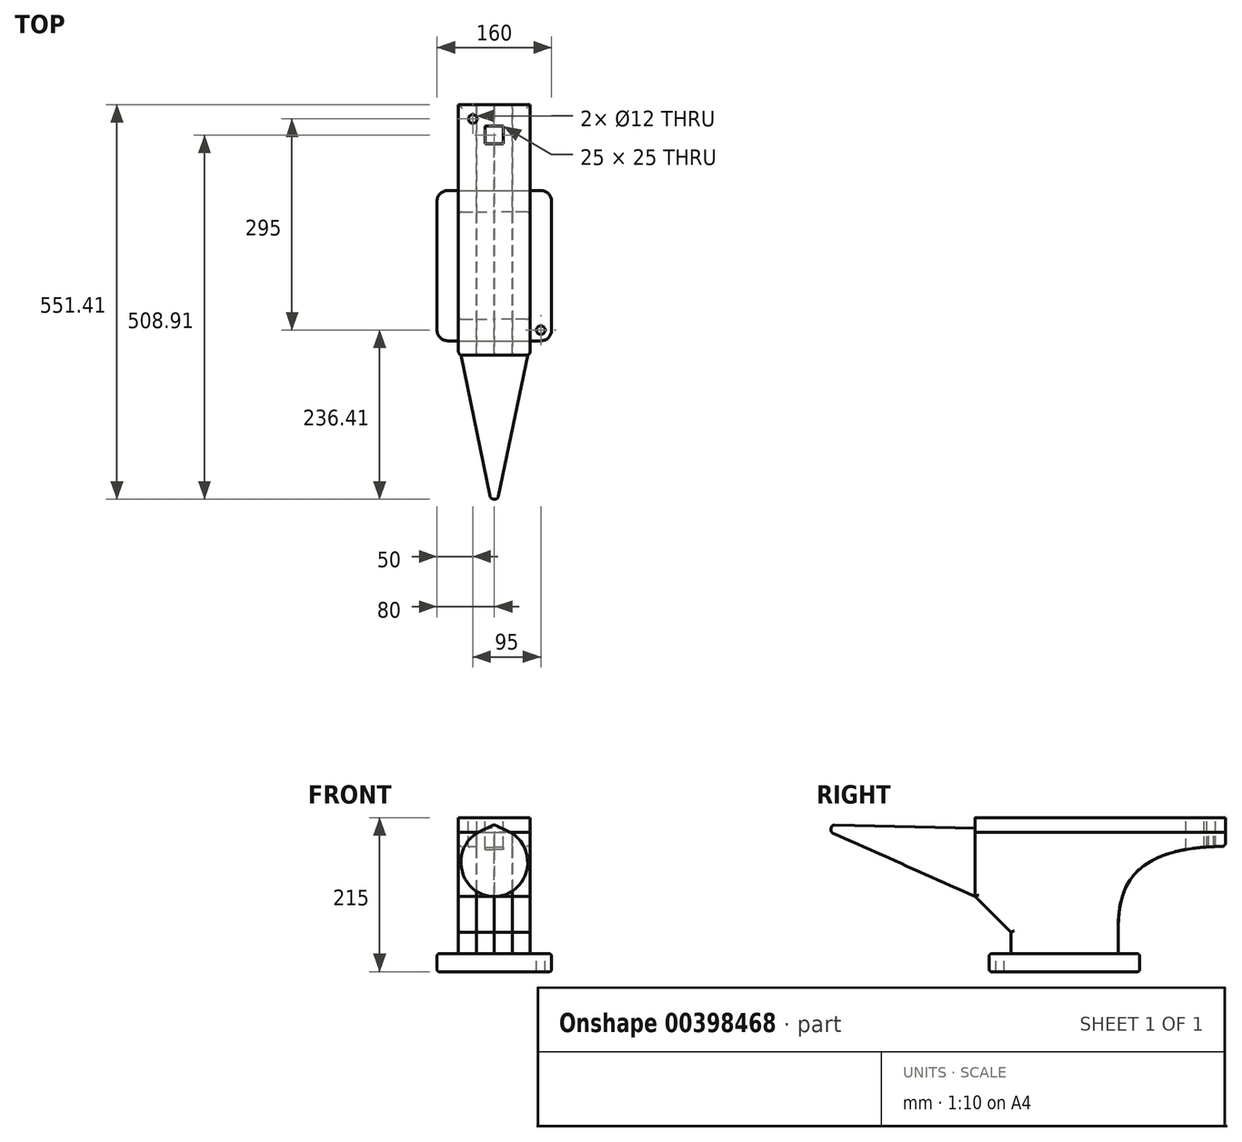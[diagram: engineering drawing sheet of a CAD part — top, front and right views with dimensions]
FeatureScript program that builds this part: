
annotation { "Feature Type Name" : "Feature", "Feature Type Description" : "" }
export const myFeature = defineFeature(function(context is Context, id is Id, definition is map)
    precondition{}
    {
        {
            var Q0;
            Q0=qCreatedBy(makeId("Right.planeOp"),FACE);
            var sketch = newSketch(context, id + "F0", { "sketchPlane" : qUnion([Q0])});
            skLineSegment(sketch, "E0", {"start": v(-75, 0) * mm, "end": v(-75, 30) * mm});
            skLineSegment(sketch, "E1", {"start": v(-75, 30) * mm, "end": v(-125, 80) * mm});
            skLineSegment(sketch, "E2", {"start": v(-125, 80) * mm, "end": v(-125, 170) * mm});
            skLineSegment(sketch, "E3", {"start": v(-125, 170) * mm, "end": v(225, 170) * mm});
            skLineSegment(sketch, "E4", {"start": v(225, 170) * mm, "end": v(225, 150) * mm});
            skLineSegment(sketch, "E5", {"start": v(75, 30) * mm, "end": v(75, 0) * mm});
            skLineSegment(sketch, "E6", {"start": v(75, 0) * mm, "end": v(-75, 0) * mm});
            skFitSpline(sketch, "E7", {"points": [v(225, 150) * mm, v(75, 30) * mm], "startDerivative": vector(-420, 0) * mm, "endDerivative": vector(0, -165) * mm});
            skSolve(sketch);
        }
        {
            var Q0;
            Q0 = qSketchRegion(id + "F0", true);
            extrude(context, id + "F1", {"entities" : qUnion([Q0]), "depth" : 25 * mm, "offsetDistance" : 25 * mm});
        }
        {
            var Q0;
            Q0=makeQuery(id+"F1.opExtrude","SWEPT_BODY",BODY,{"disambiguationData":[OSD([sQuery(id+"F0.wireOp",EDGE,"E0"),sQuery(id+"F0.wireOp",EDGE,"E1"),sQuery(id+"F0.wireOp",EDGE,"E2"),sQuery(id+"F0.wireOp",EDGE,"E3"),sQuery(id+"F0.wireOp",EDGE,"E4"),sQuery(id+"F0.wireOp",EDGE,"hNayieI8-0Q4c-M7JM-Kw2c-Cww5DPORVymM"),sQuery(id+"F0.wireOp",EDGE,"E5"),sQuery(id+"F0.wireOp",EDGE,"E6")])]});
            var Q1;
            Q1=makeQuery(id+"F1.opExtrude","SWEPT_EDGE",EDGE,{"disambiguationData":[OSD([sQuery(id+"F0.wireOp",EDGE,"E3"),sQuery(id+"F0.wireOp",EDGE,"E4")])]});
            transform(context, id + "F2", {"entities" : qUnion([Q0]), "transformType" : TransformType.TRANSLATION_ENTITY, "oppositeDirectionEntity" : true, "transformLine" : qUnion([Q1]), "makeCopy" : true});
        }
        {
            var Q0;
            Q0=makeQuery(id+"F2.opPattern","COPY",BODY,{"derivedFrom":makeQuery(id+"F1.opExtrude","SWEPT_BODY",BODY,{"disambiguationData":[OSD([sQuery(id+"F0.wireOp",EDGE,"E0"),sQuery(id+"F0.wireOp",EDGE,"E1"),sQuery(id+"F0.wireOp",EDGE,"E2"),sQuery(id+"F0.wireOp",EDGE,"E3"),sQuery(id+"F0.wireOp",EDGE,"E4"),sQuery(id+"F0.wireOp",EDGE,"hNayieI8-0Q4c-M7JM-Kw2c-Cww5DPORVymM"),sQuery(id+"F0.wireOp",EDGE,"E5"),sQuery(id+"F0.wireOp",EDGE,"E6")])]}),"instanceName":"1"});
            var Q1;
            Q1=makeQuery(id+"F1.opExtrude","SWEPT_BODY",BODY,{"disambiguationData":[OSD([sQuery(id+"F0.wireOp",EDGE,"E0"),sQuery(id+"F0.wireOp",EDGE,"E1"),sQuery(id+"F0.wireOp",EDGE,"E2"),sQuery(id+"F0.wireOp",EDGE,"E3"),sQuery(id+"F0.wireOp",EDGE,"E4"),sQuery(id+"F0.wireOp",EDGE,"hNayieI8-0Q4c-M7JM-Kw2c-Cww5DPORVymM"),sQuery(id+"F0.wireOp",EDGE,"E5"),sQuery(id+"F0.wireOp",EDGE,"E6")])]});
            var Q2;
            Q2=qCreatedBy(makeId("Right.planeOp"),FACE);
            mirror(context, id + "F3", {"entities" : qUnion([Q0, Q1]), "mirrorPlane" : qUnion([Q2])});
        }
        {
            var Q0;
            Q0=qCreatedBy(makeId("Top.planeOp"),FACE);
            var sketch = newSketch(context, id + "F4", { "sketchPlane" : qUnion([Q0])});
            skLineSegment(sketch, "E8.bottom", {"start": v(-80, -105) * mm, "end": v(80, -105) * mm});
            skLineSegment(sketch, "E8.top", {"start": v(-80, 105) * mm, "end": v(80, 105) * mm});
            skLineSegment(sketch, "E8.left", {"start": v(-80, -105) * mm, "end": v(-80, 105) * mm});
            skLineSegment(sketch, "E8.right", {"start": v(80, -105) * mm, "end": v(80, 105) * mm});
            skPoint(sketch, "E8.middle", {"position": v(0, 0) * mm});
            skSolve(sketch);
        }
        {
            var Q0;
            Q0 = qSketchRegion(id + "F4", true);
            extrude(context, id + "F5", {"entities" : qUnion([Q0]), "oppositeDirection" : true, "depth" : 25 * mm, "offsetDistance" : 25 * mm});
        }
        {
            var Q0;
            Q0=makeQuery(id+"F3.opPattern","COPY",FACE,{"derivedFrom":makeQuery(id+"F2.opPattern","COPY",FACE,{"derivedFrom":makeQuery(id+"F1.opExtrude","SWEPT_FACE",FACE,{"disambiguationData":[OSD([sQuery(id+"F0.wireOp",EDGE,"E3")])]}),"instanceName":"1"}),"instanceName":"1"});
            var sketch = newSketch(context, id + "F6", { "sketchPlane" : qUnion([Q0])});
            skLineSegment(sketch, "E9.bottom", {"start": v(-50, -125) * mm, "end": v(50, -125) * mm});
            skLineSegment(sketch, "E9.top", {"start": v(-50, 225) * mm, "end": v(50, 225) * mm});
            skLineSegment(sketch, "E9.left", {"start": v(-50, -125) * mm, "end": v(-50, 225) * mm});
            skLineSegment(sketch, "E9.right", {"start": v(50, -125) * mm, "end": v(50, 225) * mm});
            skSolve(sketch);
        }
        {
            var Q0;
            Q0 = qSketchRegion(id + "F6", true);
            extrude(context, id + "F7", {"entities" : qUnion([Q0]), "depth" : 20 * mm, "offsetDistance" : 25 * mm});
        }
        {
            var Q0;
            Q0=qCreatedBy(makeId("Right.planeOp"),FACE);
            var sketch = newSketch(context, id + "F8", { "sketchPlane" : qUnion([Q0])});
            skLineSegment(sketch, "E10", {"start": v(-125, 180) * mm, "end": v(-325, 180) * mm, "construction": true});
            skLineSegment(sketch, "E11", {"start": v(-125, 80) * mm, "end": v(-327.19, 170.24) * mm, "construction": true});
            skLineSegment(sketch, "E12", {"start": v(-327.19, 170.24) * mm, "end": v(-325, 180) * mm, "construction": true});
            skLineSegment(sketch, "E13", {"start": v(-125, 130) * mm, "end": v(-326.1, 175.12) * mm});
            skLineSegment(sketch, "E14", {"start": v(-326.1, 175.12) * mm, "end": v(-327.19, 170.24) * mm});
            skLineSegment(sketch, "E15", {"start": v(-327.19, 170.24) * mm, "end": v(-125, 80) * mm});
            skLineSegment(sketch, "E16", {"start": v(-125, 130) * mm, "end": v(-125, 80) * mm});
            skSolve(sketch);
        }
        {
            var Q0;
            Q0 = qSketchRegion(id + "F8", true);
            var Q1;
            Q1=sQuery(id+"F8.wireOp",EDGE,"E13");
            revolve(context, id + "F9", {"surfaceOperationType" : NewSurfaceOperationType.NEW, "entities" : qUnion([Q0]), "axis" : qUnion([Q1]), "revolveType" : RevolveType.FULL});
        }
        {
            var Q0;
            Q0=makeQuery(id+"F3.opPattern","COPY",BODY,{"derivedFrom":makeQuery(id+"F2.opPattern","COPY",BODY,{"derivedFrom":makeQuery(id+"F1.opExtrude","SWEPT_BODY",BODY,{"disambiguationData":[OSD([sQuery(id+"F0.wireOp",EDGE,"E0"),sQuery(id+"F0.wireOp",EDGE,"E1"),sQuery(id+"F0.wireOp",EDGE,"E2"),sQuery(id+"F0.wireOp",EDGE,"E3"),sQuery(id+"F0.wireOp",EDGE,"E4"),sQuery(id+"F0.wireOp",EDGE,"hNayieI8-0Q4c-M7JM-Kw2c-Cww5DPORVymM"),sQuery(id+"F0.wireOp",EDGE,"E5"),sQuery(id+"F0.wireOp",EDGE,"E6")])]}),"instanceName":"1"}),"instanceName":"1"});
            var Q1;
            Q1=makeQuery(id+"F3.opPattern","COPY",BODY,{"derivedFrom":makeQuery(id+"F1.opExtrude","SWEPT_BODY",BODY,{"disambiguationData":[OSD([sQuery(id+"F0.wireOp",EDGE,"E0"),sQuery(id+"F0.wireOp",EDGE,"E1"),sQuery(id+"F0.wireOp",EDGE,"E2"),sQuery(id+"F0.wireOp",EDGE,"E3"),sQuery(id+"F0.wireOp",EDGE,"E4"),sQuery(id+"F0.wireOp",EDGE,"hNayieI8-0Q4c-M7JM-Kw2c-Cww5DPORVymM"),sQuery(id+"F0.wireOp",EDGE,"E5"),sQuery(id+"F0.wireOp",EDGE,"E6")])]}),"instanceName":"1"});
            var Q2;
            Q2=makeQuery(id+"F1.opExtrude","SWEPT_BODY",BODY,{"disambiguationData":[OSD([sQuery(id+"F0.wireOp",EDGE,"E0"),sQuery(id+"F0.wireOp",EDGE,"E1"),sQuery(id+"F0.wireOp",EDGE,"E2"),sQuery(id+"F0.wireOp",EDGE,"E3"),sQuery(id+"F0.wireOp",EDGE,"E4"),sQuery(id+"F0.wireOp",EDGE,"hNayieI8-0Q4c-M7JM-Kw2c-Cww5DPORVymM"),sQuery(id+"F0.wireOp",EDGE,"E5"),sQuery(id+"F0.wireOp",EDGE,"E6")])]});
            var Q3;
            Q3=makeQuery(id+"F2.opPattern","COPY",BODY,{"derivedFrom":makeQuery(id+"F1.opExtrude","SWEPT_BODY",BODY,{"disambiguationData":[OSD([sQuery(id+"F0.wireOp",EDGE,"E0"),sQuery(id+"F0.wireOp",EDGE,"E1"),sQuery(id+"F0.wireOp",EDGE,"E2"),sQuery(id+"F0.wireOp",EDGE,"E3"),sQuery(id+"F0.wireOp",EDGE,"E4"),sQuery(id+"F0.wireOp",EDGE,"hNayieI8-0Q4c-M7JM-Kw2c-Cww5DPORVymM"),sQuery(id+"F0.wireOp",EDGE,"E5"),sQuery(id+"F0.wireOp",EDGE,"E6")])]}),"instanceName":"1"});
            var Q4;
            Q4=makeQuery(id+"F7.opExtrude","SWEPT_BODY",BODY,{"disambiguationData":[OSD([sQuery(id+"F6.wireOp",EDGE,"E9.bottom"),sQuery(id+"F6.wireOp",EDGE,"E9.top"),sQuery(id+"F6.wireOp",EDGE,"E9.left"),sQuery(id+"F6.wireOp",EDGE,"E9.right")])]});
            var Q5;
            Q5=makeQuery(id+"F9.opRevolve","SWEPT_BODY",BODY,{"disambiguationData":[OSD([sQuery(id+"F8.wireOp",EDGE,"E13"),sQuery(id+"F8.wireOp",EDGE,"E14"),sQuery(id+"F8.wireOp",EDGE,"E15"),sQuery(id+"F8.wireOp",EDGE,"E16")])]});
            booleanBodies(context, id + "F10", {"operationType" : BooleanOperationType.SUBTRACTION, "tools" : qUnion([Q0, Q1, Q2, Q3, Q4]), "targets" : qUnion([Q5]), "keepTools" : true});
        }
        {
            var Q0;
            Q0=makeQuery(id+"F5.opExtrude","CAP_FACE",FACE,{"disambiguationData":[OSD([sQuery(id+"F4.wireOp",EDGE,"E8.bottom"),sQuery(id+"F4.wireOp",EDGE,"E8.top"),sQuery(id+"F4.wireOp",EDGE,"E8.left"),sQuery(id+"F4.wireOp",EDGE,"E8.right")])],"isStart":true});
            var sketch = newSketch(context, id + "F11", { "sketchPlane" : qUnion([Q0])});
            skCircle(sketch, "E17", {"center": v(65, -90) * mm, "radius": 6 * mm});
            skSolve(sketch);
        }
        {
            var Q0;
            Q0 = qSketchRegion(id + "F11", true);
            extrude(context, id + "F12", {"entities" : qUnion([Q0]), "operationType" : NewBodyOperationType.REMOVE, "endBound" : BoundingType.THROUGH_ALL, "oppositeDirection" : true, "depth" : 25 * mm, "offsetDistance" : 25 * mm});
        }
        {
            var Q0;
            Q0=makeQuery(id+"F5.opExtrude","SWEPT_EDGE",EDGE,{"disambiguationData":[OSD([sQuery(id+"F4.wireOp",EDGE,"E8.top"),sQuery(id+"F4.wireOp",EDGE,"E8.right")])]});
            var Q1;
            Q1=makeQuery(id+"F5.opExtrude","SWEPT_EDGE",EDGE,{"disambiguationData":[OSD([sQuery(id+"F4.wireOp",EDGE,"E8.bottom"),sQuery(id+"F4.wireOp",EDGE,"E8.right")])]});
            var Q2;
            Q2=makeQuery(id+"F5.opExtrude","SWEPT_EDGE",EDGE,{"disambiguationData":[OSD([sQuery(id+"F4.wireOp",EDGE,"E8.top"),sQuery(id+"F4.wireOp",EDGE,"E8.left")])]});
            var Q3;
            Q3=makeQuery(id+"F5.opExtrude","SWEPT_EDGE",EDGE,{"disambiguationData":[OSD([sQuery(id+"F4.wireOp",EDGE,"E8.bottom"),sQuery(id+"F4.wireOp",EDGE,"E8.left")])]});
            fillet(context, id + "F13", {"entities" : qUnion([Q0, Q1, Q2, Q3]), "tangentPropagation" : true, "radius" : 15 * mm, "defaultsChanged" : true, "vertexSettings" : [], "allowEdgeOverflow" : false});
        }
        {
            var Q0;
            Q0=makeQuery(id+"F5.opExtrude","CAP_EDGE",EDGE,{"disambiguationData":[OSD([sQuery(id+"F4.wireOp",EDGE,"E8.right")])],"isStart":true});
            var Q1;
            Q1=makeQuery(id+"F5.opExtrude","CAP_EDGE",EDGE,{"disambiguationData":[OSD([sQuery(id+"F4.wireOp",EDGE,"E8.bottom")])],"isStart":true});
            var Q2;
            Q2=makeQuery(id+"F5.opExtrude","CAP_EDGE",EDGE,{"disambiguationData":[OSD([sQuery(id+"F4.wireOp",EDGE,"E8.top")])],"isStart":true});
            var Q3;
            Q3=makeQuery(id+"F5.opExtrude","CAP_EDGE",EDGE,{"disambiguationData":[OSD([sQuery(id+"F4.wireOp",EDGE,"E8.left")])],"isStart":true});
            var Q4;
            Q4=makeQuery(id+"F5.opExtrude","CAP_EDGE",EDGE,{"disambiguationData":[OSD([sQuery(id+"F4.wireOp",EDGE,"E8.right")])],"isStart":false});
            var Q5;
            Q5=makeQuery(id+"F5.opExtrude","CAP_EDGE",EDGE,{"disambiguationData":[OSD([sQuery(id+"F4.wireOp",EDGE,"E8.top")])],"isStart":false});
            var Q6;
            Q6=makeQuery(id+"F5.opExtrude","CAP_EDGE",EDGE,{"disambiguationData":[OSD([sQuery(id+"F4.wireOp",EDGE,"E8.bottom")])],"isStart":false});
            var Q7;
            Q7=makeQuery(id+"F5.opExtrude","CAP_EDGE",EDGE,{"disambiguationData":[OSD([sQuery(id+"F4.wireOp",EDGE,"E8.left")])],"isStart":false});
            fillet(context, id + "F14", {"entities" : qUnion([Q0, Q1, Q2, Q3, Q4, Q5, Q6, Q7]), "tangentPropagation" : true, "radius" : 3 * mm, "defaultsChanged" : true, "vertexSettings" : [], "allowEdgeOverflow" : false});
        }
        {
            var Q0;
            Q0=makeQuery(id+"F3.opPattern","COPY",EDGE,{"derivedFrom":makeQuery(id+"F2.opPattern","COPY",EDGE,{"derivedFrom":makeQuery(id+"F1.opExtrude","CAP_EDGE",EDGE,{"disambiguationData":[OSD([sQuery(id+"F0.wireOp",EDGE,"E7")])],"isStart":false}),"instanceName":"1"}),"instanceName":"1"});
            var Q1;
            Q1=makeQuery(id+"F2.opPattern","COPY",EDGE,{"derivedFrom":makeQuery(id+"F1.opExtrude","CAP_EDGE",EDGE,{"disambiguationData":[OSD([sQuery(id+"F0.wireOp",EDGE,"E7")])],"isStart":false}),"instanceName":"1"});
            var Q2;
            Q2=makeQuery(id+"F2.opPattern","COPY",EDGE,{"derivedFrom":makeQuery(id+"F1.opExtrude","SWEPT_EDGE",EDGE,{"disambiguationData":[OSD([sQuery(id+"F0.wireOp",EDGE,"E4"),sQuery(id+"F0.wireOp",EDGE,"E7")])]}),"instanceName":"1"});
            var Q3;
            Q3=makeQuery(id+"F1.opExtrude","SWEPT_EDGE",EDGE,{"disambiguationData":[OSD([sQuery(id+"F0.wireOp",EDGE,"E4"),sQuery(id+"F0.wireOp",EDGE,"E7")])]});
            var Q4;
            Q4=makeQuery(id+"F3.opPattern","COPY",EDGE,{"derivedFrom":makeQuery(id+"F1.opExtrude","SWEPT_EDGE",EDGE,{"disambiguationData":[OSD([sQuery(id+"F0.wireOp",EDGE,"E4"),sQuery(id+"F0.wireOp",EDGE,"E7")])]}),"instanceName":"1"});
            var Q5;
            Q5=makeQuery(id+"F3.opPattern","COPY",EDGE,{"derivedFrom":makeQuery(id+"F2.opPattern","COPY",EDGE,{"derivedFrom":makeQuery(id+"F1.opExtrude","SWEPT_EDGE",EDGE,{"disambiguationData":[OSD([sQuery(id+"F0.wireOp",EDGE,"E4"),sQuery(id+"F0.wireOp",EDGE,"E7")])]}),"instanceName":"1"}),"instanceName":"1"});
            var Q6;
            Q6=makeQuery(id+"F2.opPattern","COPY",EDGE,{"derivedFrom":makeQuery(id+"F1.opExtrude","CAP_EDGE",EDGE,{"disambiguationData":[OSD([sQuery(id+"F0.wireOp",EDGE,"E0")])],"isStart":false}),"instanceName":"1"});
            var Q7;
            Q7=makeQuery(id+"F2.opPattern","COPY",EDGE,{"derivedFrom":makeQuery(id+"F1.opExtrude","CAP_EDGE",EDGE,{"disambiguationData":[OSD([sQuery(id+"F0.wireOp",EDGE,"E1")])],"isStart":false}),"instanceName":"1"});
            var Q8;
            Q8=makeQuery(id+"F2.opPattern","COPY",EDGE,{"derivedFrom":makeQuery(id+"F1.opExtrude","CAP_EDGE",EDGE,{"disambiguationData":[OSD([sQuery(id+"F0.wireOp",EDGE,"E2")])],"isStart":false}),"instanceName":"1"});
            var Q9;
            Q9=makeQuery(id+"F7.opExtrude","SWEPT_EDGE",EDGE,{"disambiguationData":[OSD([sQuery(id+"F6.wireOp",EDGE,"E9.bottom"),sQuery(id+"F6.wireOp",EDGE,"E9.right")])]});
            var Q10;
            Q10=makeQuery(id+"F3.opPattern","COPY",EDGE,{"derivedFrom":makeQuery(id+"F2.opPattern","COPY",EDGE,{"derivedFrom":makeQuery(id+"F1.opExtrude","CAP_EDGE",EDGE,{"disambiguationData":[OSD([sQuery(id+"F0.wireOp",EDGE,"E0")])],"isStart":false}),"instanceName":"1"}),"instanceName":"1"});
            var Q11;
            Q11=makeQuery(id+"F3.opPattern","COPY",EDGE,{"derivedFrom":makeQuery(id+"F2.opPattern","COPY",EDGE,{"derivedFrom":makeQuery(id+"F1.opExtrude","CAP_EDGE",EDGE,{"disambiguationData":[OSD([sQuery(id+"F0.wireOp",EDGE,"E1")])],"isStart":false}),"instanceName":"1"}),"instanceName":"1"});
            var Q12;
            Q12=makeQuery(id+"F3.opPattern","COPY",EDGE,{"derivedFrom":makeQuery(id+"F2.opPattern","COPY",EDGE,{"derivedFrom":makeQuery(id+"F1.opExtrude","CAP_EDGE",EDGE,{"disambiguationData":[OSD([sQuery(id+"F0.wireOp",EDGE,"E2")])],"isStart":false}),"instanceName":"1"}),"instanceName":"1"});
            var Q13;
            Q13=makeQuery(id+"F7.opExtrude","SWEPT_EDGE",EDGE,{"disambiguationData":[OSD([sQuery(id+"F6.wireOp",EDGE,"E9.bottom"),sQuery(id+"F6.wireOp",EDGE,"E9.left")])]});
            var Q14;
            Q14=makeQuery(id+"F9.opRevolve","SWEPT_EDGE",EDGE,{"disambiguationData":[OSD([sQuery(id+"F8.wireOp",EDGE,"E14"),sQuery(id+"F8.wireOp",EDGE,"E15")])]});
            fillet(context, id + "F15", {"entities" : qUnion([Q0, Q1, Q2, Q3, Q4, Q5, Q6, Q7, Q8, Q9, Q10, Q11, Q12, Q13, Q14]), "tangentPropagation" : true, "radius" : 5 * mm, "defaultsChanged" : false, "vertexSettings" : [], "allowEdgeOverflow" : false});
        }
        {
            var Q0;
            Q0=makeQuery(id+"F7.opExtrude","CAP_FACE",FACE,{"disambiguationData":[OSD([sQuery(id+"F6.wireOp",EDGE,"E9.bottom"),sQuery(id+"F6.wireOp",EDGE,"E9.top"),sQuery(id+"F6.wireOp",EDGE,"E9.left"),sQuery(id+"F6.wireOp",EDGE,"E9.right")])],"isStart":false});
            var sketch = newSketch(context, id + "F16", { "sketchPlane" : qUnion([Q0])});
            skLineSegment(sketch, "E18.bottom", {"start": v(-12.5, 170) * mm, "end": v(12.5, 170) * mm});
            skLineSegment(sketch, "E18.top", {"start": v(-12.5, 195) * mm, "end": v(12.5, 195) * mm});
            skLineSegment(sketch, "E18.left", {"start": v(-12.5, 170) * mm, "end": v(-12.5, 195) * mm});
            skLineSegment(sketch, "E18.right", {"start": v(12.5, 170) * mm, "end": v(12.5, 195) * mm});
            skPoint(sketch, "E18.middle", {"position": v(0, 182.5) * mm});
            skSolve(sketch);
        }
        {
            var Q0;
            Q0 = qSketchRegion(id + "F16", true);
            extrude(context, id + "F17", {"entities" : qUnion([Q0]), "operationType" : NewBodyOperationType.REMOVE, "endBound" : BoundingType.THROUGH_ALL, "oppositeDirection" : true, "depth" : 25 * mm, "offsetDistance" : 25 * mm});
        }
        {
            var Q0;
            Q0=makeQuery(id+"F7.opExtrude","CAP_FACE",FACE,{"disambiguationData":[OSD([sQuery(id+"F6.wireOp",EDGE,"E9.bottom"),sQuery(id+"F6.wireOp",EDGE,"E9.top"),sQuery(id+"F6.wireOp",EDGE,"E9.left"),sQuery(id+"F6.wireOp",EDGE,"E9.right")])],"isStart":false});
            var sketch = newSketch(context, id + "F18", { "sketchPlane" : qUnion([Q0])});
            skCircle(sketch, "E19", {"center": v(-30, 205) * mm, "radius": 6 * mm});
            skSolve(sketch);
        }
        {
            var Q0;
            Q0 = qSketchRegion(id + "F18", true);
            extrude(context, id + "F19", {"entities" : qUnion([Q0]), "operationType" : NewBodyOperationType.REMOVE, "endBound" : BoundingType.THROUGH_ALL, "oppositeDirection" : true, "depth" : 25 * mm, "offsetDistance" : 25 * mm});
        }
    });
